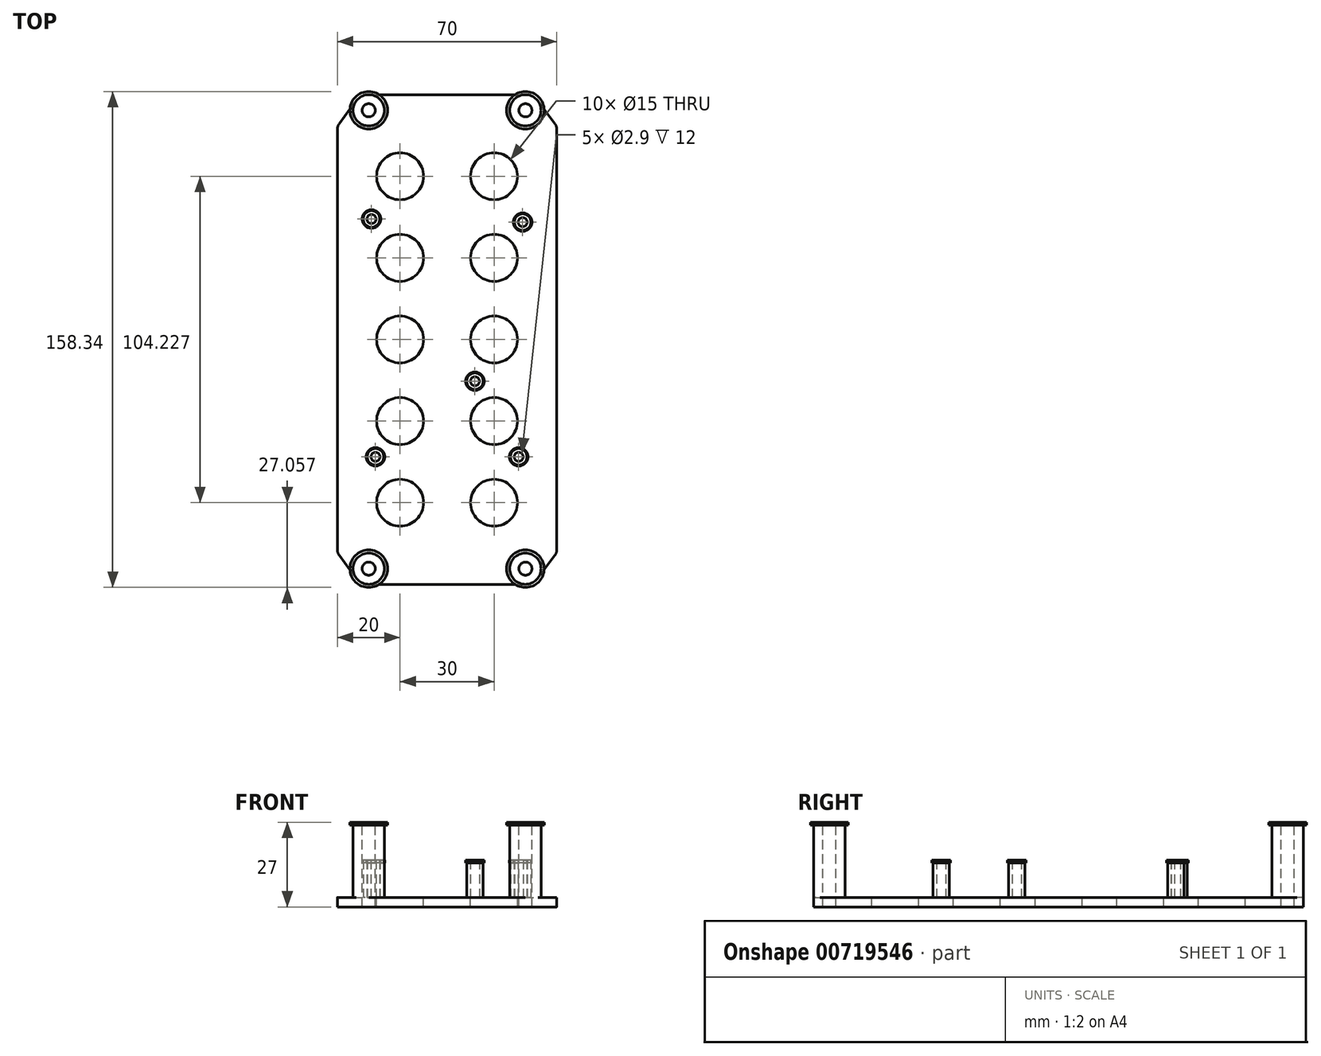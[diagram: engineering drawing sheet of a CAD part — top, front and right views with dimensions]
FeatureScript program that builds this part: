
annotation { "Feature Type Name" : "Feature", "Feature Type Description" : "" }
export const myFeature = defineFeature(function(context is Context, id is Id, definition is map)
    precondition{}
    {
        {
            var Q0;
            Q0=qCreatedBy(makeId("Top.planeOp"),FACE);
            var sketch = newSketch(context, id + "F0", { "sketchPlane" : qUnion([Q0])});
            skLineSegment(sketch, "E0.bottom", {"start": v(0, 0) * mm, "end": v(70, 0) * mm});
            skLineSegment(sketch, "E0.top", {"start": v(0, 136.34) * mm, "end": v(70, 136.34) * mm});
            skLineSegment(sketch, "E0.left", {"start": v(0, 0) * mm, "end": v(0, 136.34) * mm});
            skLineSegment(sketch, "E0.right", {"start": v(70, 0) * mm, "end": v(70, 136.34) * mm});
            skPoint(sketch, "E1", {"position": v(10.87, 106.64) * mm});
            skPoint(sketch, "E2", {"position": v(59.13, 105.64) * mm});
            skPoint(sketch, "E3", {"position": v(43.9, 54.84) * mm});
            skPoint(sketch, "E4", {"position": v(57.86, 30.71) * mm});
            skPoint(sketch, "E5", {"position": v(12.14, 30.71) * mm});
            skCircle(sketch, "E6", {"center": v(10.87, 106.64) * mm, "radius": 2.65 * mm});
            skCircle(sketch, "E7", {"center": v(59.13, 105.64) * mm, "radius": 2.65 * mm});
            skCircle(sketch, "E8", {"center": v(43.9, 54.84) * mm, "radius": 2.65 * mm});
            skCircle(sketch, "E9", {"center": v(12.14, 30.71) * mm, "radius": 2.65 * mm});
            skCircle(sketch, "E10", {"center": v(57.86, 30.71) * mm, "radius": 2.65 * mm});
            skCircle(sketch, "E11", {"center": v(10.87, 106.64) * mm, "radius": 1.45 * mm});
            skCircle(sketch, "E12", {"center": v(59.13, 105.64) * mm, "radius": 1.45 * mm});
            skCircle(sketch, "E13", {"center": v(43.9, 54.84) * mm, "radius": 1.45 * mm});
            skCircle(sketch, "E14", {"center": v(57.86, 30.71) * mm, "radius": 1.45 * mm});
            skCircle(sketch, "E15", {"center": v(12.14, 30.71) * mm, "radius": 1.45 * mm});
            skLineSegment(sketch, "E16.bottom", {"start": v(10.87, 106.64) * mm, "end": v(0, 106.64) * mm});
            skLineSegment(sketch, "E16.top", {"start": v(10.87, 106.64) * mm, "end": v(0, 106.64) * mm});
            skLineSegment(sketch, "E16.left", {"start": v(10.87, 106.64) * mm, "end": v(10.87, 106.64) * mm});
            skLineSegment(sketch, "E16.right", {"start": v(0, 106.64) * mm, "end": v(0, 106.64) * mm});
            skLineSegment(sketch, "E17", {"start": v(59.13, 105.64) * mm, "end": v(70, 105.64) * mm});
            skLineSegment(sketch, "E18", {"start": v(12.14, 30.71) * mm, "end": v(0, 30.71) * mm});
            skLineSegment(sketch, "E19", {"start": v(57.86, 30.71) * mm, "end": v(70, 30.71) * mm});
            skCircle(sketch, "E20", {"center": v(10, 141.34) * mm, "radius": 5 * mm});
            skCircle(sketch, "E21", {"center": v(60, 141.34) * mm, "radius": 5 * mm});
            skLineSegment(sketch, "E22", {"start": v(0, 136.34) * mm, "end": v(6, 144.34) * mm});
            skLineSegment(sketch, "E23", {"start": v(70, 136.34) * mm, "end": v(64, 144.34) * mm});
            skLineSegment(sketch, "E24", {"start": v(10, 146.34) * mm, "end": v(60, 146.34) * mm});
            skCircle(sketch, "E25", {"center": v(10, -5) * mm, "radius": 5 * mm});
            skCircle(sketch, "E26", {"center": v(60, -5) * mm, "radius": 5 * mm});
            skLineSegment(sketch, "E27", {"start": v(0, 0) * mm, "end": v(6, -8) * mm});
            skLineSegment(sketch, "E28", {"start": v(70, 0) * mm, "end": v(64, -8) * mm});
            skLineSegment(sketch, "E29", {"start": v(10, -10) * mm, "end": v(60, -10) * mm});
            skCircle(sketch, "E30", {"center": v(10, 141.34) * mm, "radius": 2.1 * mm});
            skCircle(sketch, "E31", {"center": v(60, 141.34) * mm, "radius": 2.1 * mm});
            skCircle(sketch, "E32", {"center": v(10, -5) * mm, "radius": 2.1 * mm});
            skCircle(sketch, "E33", {"center": v(60, -5) * mm, "radius": 2.1 * mm});
            skSolve(sketch);
        }
        {
            var Q0;
            Q0=makeQuery(id+"F0.imprint","IMPRINT",FACE,{"disambiguationData":[TD([[makeQuery(id+"F0.imprint","IMPRINT",EDGE,{"derivedFrom":sQuery(id+"F0.wireOp",EDGE,"5M5isl8t-deyZ-40FD-1slN-9rMmY2fGWf6l")}),-1.0]])]});
            var Q1;
            {var subQ1=sQuery(id+"F0.wireOp",EDGE,"E0.left");Q1=makeQuery(id+"F0.imprint","IMPRINT",FACE,{"disambiguationData":[TD([[makeQuery(id+"F0.imprint","IMPRINT",EDGE,{"derivedFrom":subQ1}),-1.0]])]});}
            var Q2;
            {var subQ0=sQuery(id+"F0.wireOp",EDGE,"ZGELtEtJ-xnq0-4358-XdRx-OSzrZUhgYs4m");Q2=makeQuery(id+"F0.imprint","IMPRINT",FACE,{"disambiguationData":[TD([[makeQuery(id+"F0.imprint","IMPRINT",EDGE,{"derivedFrom":subQ0}),-1.0]])]});}
            var Q3;
            {var subQ0=sQuery(id+"F0.wireOp",EDGE,"XsqxNTd2-7exo-Mk4u-Frq7-MKPhXaLccWfz");Q3=makeQuery(id+"F0.imprint","IMPRINT",FACE,{"disambiguationData":[TD([[makeQuery(id+"F0.imprint","IMPRINT",EDGE,{"derivedFrom":subQ0}),-1.0]])]});}
            var Q4;
            {var subQ0=sQuery(id+"F0.wireOp",EDGE,"Y27PalPK-6cuN-ouRf-MoMI-afCK04gGz7O5");Q4=makeQuery(id+"F0.imprint","IMPRINT",FACE,{"disambiguationData":[TD([[makeQuery(id+"F0.imprint","IMPRINT",EDGE,{"derivedFrom":subQ0}),1.0]])]});}
            var Q5;
            Q5=makeQuery(id+"F0.imprint","IMPRINT",FACE,{"disambiguationData":[TD([[makeQuery(id+"F0.imprint","IMPRINT",EDGE,{"derivedFrom":sQuery(id+"F0.wireOp",EDGE,"YguYaOqL-j1yr-7eBz-XWkk-AffqH1J2VJiA")}),-1.0]])]});
            var Q6;
            {var subQ0=sQuery(id+"F0.wireOp",EDGE,"ZxH4SoS6-8SnG-QbFF-Vepe-AWZUzMMQzlqZ");Q6=makeQuery(id+"F0.imprint","IMPRINT",FACE,{"disambiguationData":[TD([[makeQuery(id+"F0.imprint","IMPRINT",EDGE,{"derivedFrom":subQ0}),-1.0]])]});}
            var Q7;
            Q7=makeQuery(id+"F0.imprint","IMPRINT",FACE,{"disambiguationData":[TD([[makeQuery(id+"F0.imprint","IMPRINT",EDGE,{"derivedFrom":sQuery(id+"F0.wireOp",EDGE,"E9")}),1.0]])]});
            var Q8;
            Q8=makeQuery(id+"F0.imprint","IMPRINT",FACE,{"disambiguationData":[TD([[makeQuery(id+"F0.imprint","IMPRINT",EDGE,{"derivedFrom":sQuery(id+"F0.wireOp",EDGE,"E7")}),1.0]])]});
            var Q9;
            Q9=makeQuery(id+"F0.imprint","IMPRINT",FACE,{"disambiguationData":[TD([[makeQuery(id+"F0.imprint","IMPRINT",EDGE,{"derivedFrom":sQuery(id+"F0.wireOp",EDGE,"E8")}),1.0]])]});
            var Q10;
            Q10=makeQuery(id+"F0.imprint","IMPRINT",FACE,{"disambiguationData":[TD([[makeQuery(id+"F0.imprint","IMPRINT",EDGE,{"derivedFrom":sQuery(id+"F0.wireOp",EDGE,"E10")}),1.0]])]});
            var Q11;
            Q11=makeQuery(id+"F0.imprint","IMPRINT",FACE,{"disambiguationData":[TD([[makeQuery(id+"F0.imprint","IMPRINT",EDGE,{"derivedFrom":sQuery(id+"F0.wireOp",EDGE,"E6")}),1.0]])]});
            var Q12;
            Q12=makeQuery(id+"F0.imprint","IMPRINT",FACE,{"disambiguationData":[TD([[makeQuery(id+"F0.imprint","IMPRINT",EDGE,{"derivedFrom":sQuery(id+"F0.wireOp",EDGE,"E11")}),1.0]])]});
            var Q13;
            Q13=makeQuery(id+"F0.imprint","IMPRINT",FACE,{"disambiguationData":[TD([[makeQuery(id+"F0.imprint","IMPRINT",EDGE,{"derivedFrom":sQuery(id+"F0.wireOp",EDGE,"E15")}),1.0]])]});
            var Q14;
            Q14=makeQuery(id+"F0.imprint","IMPRINT",FACE,{"disambiguationData":[TD([[makeQuery(id+"F0.imprint","IMPRINT",EDGE,{"derivedFrom":sQuery(id+"F0.wireOp",EDGE,"E12")}),1.0]])]});
            var Q15;
            Q15=makeQuery(id+"F0.imprint","IMPRINT",FACE,{"disambiguationData":[TD([[makeQuery(id+"F0.imprint","IMPRINT",EDGE,{"derivedFrom":sQuery(id+"F0.wireOp",EDGE,"E14")}),1.0]])]});
            var Q16;
            Q16=makeQuery(id+"F0.imprint","IMPRINT",FACE,{"disambiguationData":[TD([[makeQuery(id+"F0.imprint","IMPRINT",EDGE,{"derivedFrom":sQuery(id+"F0.wireOp",EDGE,"E13")}),1.0]])]});
            var Q17;
            {var subQ5=sQuery(id+"F0.wireOp",EDGE,"E24");Q17=makeQuery(id+"F0.imprint","IMPRINT",FACE,{"disambiguationData":[TD([[makeQuery(id+"F0.imprint","IMPRINT",EDGE,{"derivedFrom":subQ5}),-1.0]])]});}
            var Q18;
            {var subQ0=sQuery(id+"F0.wireOp",EDGE,"E22");Q18=makeQuery(id+"F0.imprint","IMPRINT",FACE,{"disambiguationData":[TD([[makeQuery(id+"F0.imprint","IMPRINT",EDGE,{"derivedFrom":subQ0}),-1.0]])]});}
            var Q19;
            {var subQ0=sQuery(id+"F0.wireOp",EDGE,"E20");var subQ1=makeQuery(id+"F0.imprint","INTERSECT",VERTEX,{"derivedFrom":[subQ0,sQuery(id+"F0.wireOp",EDGE,"E22")]});Q19=makeQuery(id+"F0.imprint","IMPRINT",FACE,{"disambiguationData":[TD([[makeQuery(id+"F0.imprint","IMPRINT",EDGE,{"disambiguationData":[TD([[subQ1,1.0]])],"derivedFrom":subQ0}),1.0]])]});}
            var Q20;
            {var subQ0=sQuery(id+"F0.wireOp",EDGE,"E21");var subQ1=makeQuery(id+"F0.imprint","INTERSECT",VERTEX,{"derivedFrom":[subQ0,sQuery(id+"F0.wireOp",EDGE,"E23")]});Q20=makeQuery(id+"F0.imprint","IMPRINT",FACE,{"disambiguationData":[TD([[makeQuery(id+"F0.imprint","IMPRINT",EDGE,{"disambiguationData":[TD([[subQ1,-1.0]])],"derivedFrom":subQ0}),1.0]])]});}
            var Q21;
            {var subQ0=sQuery(id+"F0.wireOp",EDGE,"E23");Q21=makeQuery(id+"F0.imprint","IMPRINT",FACE,{"disambiguationData":[TD([[makeQuery(id+"F0.imprint","IMPRINT",EDGE,{"derivedFrom":subQ0}),1.0]])]});}
            var Q22;
            {var subQ0=sQuery(id+"F0.wireOp",EDGE,"E28");Q22=makeQuery(id+"F0.imprint","IMPRINT",FACE,{"disambiguationData":[TD([[makeQuery(id+"F0.imprint","IMPRINT",EDGE,{"derivedFrom":subQ0}),-1.0]])]});}
            var Q23;
            {var subQ0=sQuery(id+"F0.wireOp",EDGE,"E26");var subQ1=makeQuery(id+"F0.imprint","INTERSECT",VERTEX,{"derivedFrom":[subQ0,sQuery(id+"F0.wireOp",EDGE,"E29")]});Q23=makeQuery(id+"F0.imprint","IMPRINT",FACE,{"disambiguationData":[TD([[makeQuery(id+"F0.imprint","IMPRINT",EDGE,{"disambiguationData":[TD([[subQ1,1.0]])],"derivedFrom":subQ0}),1.0]])]});}
            var Q24;
            {var subQ5=sQuery(id+"F0.wireOp",EDGE,"E29");Q24=makeQuery(id+"F0.imprint","IMPRINT",FACE,{"disambiguationData":[TD([[makeQuery(id+"F0.imprint","IMPRINT",EDGE,{"derivedFrom":subQ5}),1.0]])]});}
            var Q25;
            {var subQ0=sQuery(id+"F0.wireOp",EDGE,"E25");var subQ1=makeQuery(id+"F0.imprint","INTERSECT",VERTEX,{"derivedFrom":[subQ0,sQuery(id+"F0.wireOp",EDGE,"E27")]});Q25=makeQuery(id+"F0.imprint","IMPRINT",FACE,{"disambiguationData":[TD([[makeQuery(id+"F0.imprint","IMPRINT",EDGE,{"disambiguationData":[TD([[subQ1,1.0]])],"derivedFrom":subQ0}),1.0]])]});}
            var Q26;
            {var subQ0=sQuery(id+"F0.wireOp",EDGE,"E27");Q26=makeQuery(id+"F0.imprint","IMPRINT",FACE,{"disambiguationData":[TD([[makeQuery(id+"F0.imprint","IMPRINT",EDGE,{"derivedFrom":subQ0}),1.0]])]});}
            extrude(context, id + "F1", {"entities" : qUnion([Q0, Q1, Q2, Q3, Q4, Q5, Q6, Q7, Q8, Q9, Q10, Q11, Q12, Q13, Q14, Q15, Q16, Q17, Q18, Q19, Q20, Q21, Q22, Q23, Q24, Q25, Q26]), "oppositeDirection" : true, "depth" : 3 * mm, "offsetDistance" : 25 * mm});
        }
        {
            var Q0;
            Q0=makeQuery(id+"F0.imprint","IMPRINT",FACE,{"disambiguationData":[TD([[makeQuery(id+"F0.imprint","IMPRINT",EDGE,{"derivedFrom":sQuery(id+"F0.wireOp",EDGE,"E9")}),1.0]])]});
            var Q1;
            Q1=makeQuery(id+"F0.imprint","IMPRINT",FACE,{"disambiguationData":[TD([[makeQuery(id+"F0.imprint","IMPRINT",EDGE,{"derivedFrom":sQuery(id+"F0.wireOp",EDGE,"E8")}),1.0]])]});
            var Q2;
            Q2=makeQuery(id+"F0.imprint","IMPRINT",FACE,{"disambiguationData":[TD([[makeQuery(id+"F0.imprint","IMPRINT",EDGE,{"derivedFrom":sQuery(id+"F0.wireOp",EDGE,"E10")}),1.0]])]});
            var Q3;
            Q3=makeQuery(id+"F0.imprint","IMPRINT",FACE,{"disambiguationData":[TD([[makeQuery(id+"F0.imprint","IMPRINT",EDGE,{"derivedFrom":sQuery(id+"F0.wireOp",EDGE,"E6")}),1.0]])]});
            var Q4;
            Q4=makeQuery(id+"F0.imprint","IMPRINT",FACE,{"disambiguationData":[TD([[makeQuery(id+"F0.imprint","IMPRINT",EDGE,{"derivedFrom":sQuery(id+"F0.wireOp",EDGE,"E7")}),1.0]])]});
            extrude(context, id + "F2", {"entities" : qUnion([Q0, Q1, Q2, Q3, Q4]), "operationType" : NewBodyOperationType.ADD, "depth" : 12 * mm, "offsetDistance" : 25 * mm});
        }
        {
            var Q0;
            Q0=makeQuery(id+"F0.imprint","IMPRINT",FACE,{"disambiguationData":[TD([[makeQuery(id+"F0.imprint","IMPRINT",EDGE,{"derivedFrom":sQuery(id+"F0.wireOp",EDGE,"E30")}),-1.0]])]});
            var Q1;
            Q1=makeQuery(id+"F0.imprint","IMPRINT",FACE,{"disambiguationData":[TD([[makeQuery(id+"F0.imprint","IMPRINT",EDGE,{"derivedFrom":sQuery(id+"F0.wireOp",EDGE,"E31")}),-1.0]])]});
            var Q2;
            Q2=makeQuery(id+"F0.imprint","IMPRINT",FACE,{"disambiguationData":[TD([[makeQuery(id+"F0.imprint","IMPRINT",EDGE,{"derivedFrom":sQuery(id+"F0.wireOp",EDGE,"E32")}),-1.0]])]});
            var Q3;
            Q3=makeQuery(id+"F0.imprint","IMPRINT",FACE,{"disambiguationData":[TD([[makeQuery(id+"F0.imprint","IMPRINT",EDGE,{"derivedFrom":sQuery(id+"F0.wireOp",EDGE,"E33")}),-1.0]])]});
            extrude(context, id + "F3", {"entities" : qUnion([Q0, Q1, Q2, Q3]), "operationType" : NewBodyOperationType.ADD, "depth" : 24 * mm, "offsetDistance" : 25 * mm});
        }
        {
            var Q0;
            Q0=qCreatedBy(makeId("Top.planeOp"),FACE);
            var sketch = newSketch(context, id + "F4", { "sketchPlane" : qUnion([Q0])});
            skLineSegment(sketch, "E34.0", {"start": v(0, 136.34) * mm, "end": v(70, 136.34) * mm});
            skLineSegment(sketch, "E35.0", {"start": v(0, 0) * mm, "end": v(0, 136.34) * mm});
            skLineSegment(sketch, "E36.0", {"start": v(70, 0) * mm, "end": v(70, 136.34) * mm});
            skPoint(sketch, "E37", {"position": v(20, 120.28) * mm});
            skPoint(sketch, "E38", {"position": v(50, 120.28) * mm});
            skPoint(sketch, "E39", {"position": v(50, 68.17) * mm});
            skPoint(sketch, "E40", {"position": v(50, 42.11) * mm});
            skPoint(sketch, "E41", {"position": v(20, 68.17) * mm});
            skPoint(sketch, "E42", {"position": v(20, 42.11) * mm});
            skPoint(sketch, "E43", {"position": v(20, 16.06) * mm});
            skPoint(sketch, "E44", {"position": v(50, 16.06) * mm});
            skLineSegment(sketch, "E45", {"start": v(20, 68.17) * mm, "end": v(20, 42.11) * mm});
            skLineSegment(sketch, "E46", {"start": v(20, 42.11) * mm, "end": v(20, 16.06) * mm});
            skLineSegment(sketch, "E47", {"start": v(50, 16.06) * mm, "end": v(50, 42.11) * mm});
            skLineSegment(sketch, "E48", {"start": v(50, 68.17) * mm, "end": v(50, 42.11) * mm});
            skPoint(sketch, "E49", {"position": v(20, 94.23) * mm});
            skPoint(sketch, "E50", {"position": v(50, 94.23) * mm});
            skLineSegment(sketch, "E51", {"start": v(50, 120.28) * mm, "end": v(50, 94.23) * mm});
            skLineSegment(sketch, "E52", {"start": v(50, 68.17) * mm, "end": v(50, 94.23) * mm});
            skLineSegment(sketch, "E53", {"start": v(20, 94.23) * mm, "end": v(20, 68.17) * mm});
            skLineSegment(sketch, "E54", {"start": v(20, 94.23) * mm, "end": v(20, 120.28) * mm});
            skCircle(sketch, "E55", {"center": v(20, 120.28) * mm, "radius": 7.5 * mm});
            skCircle(sketch, "E56", {"center": v(50, 120.28) * mm, "radius": 7.5 * mm});
            skCircle(sketch, "E57", {"center": v(50, 94.23) * mm, "radius": 7.5 * mm});
            skCircle(sketch, "E58", {"center": v(20, 94.23) * mm, "radius": 7.5 * mm});
            skCircle(sketch, "E59", {"center": v(20, 68.17) * mm, "radius": 7.5 * mm});
            skCircle(sketch, "E60", {"center": v(50, 68.17) * mm, "radius": 7.5 * mm});
            skCircle(sketch, "E61", {"center": v(20, 42.11) * mm, "radius": 7.5 * mm});
            skCircle(sketch, "E62", {"center": v(50, 42.11) * mm, "radius": 7.5 * mm});
            skCircle(sketch, "E63", {"center": v(20, 16.06) * mm, "radius": 7.5 * mm});
            skCircle(sketch, "E64", {"center": v(50, 16.06) * mm, "radius": 7.5 * mm});
            skLineSegment(sketch, "E65", {"start": v(50, 120.28) * mm, "end": v(50, 146.34) * mm});
            skLineSegment(sketch, "E66", {"start": v(20, 120.28) * mm, "end": v(20, 146.34) * mm});
            skLineSegment(sketch, "E67", {"start": v(50, 16.06) * mm, "end": v(50, -10) * mm});
            skLineSegment(sketch, "E68", {"start": v(20, 16.06) * mm, "end": v(20, -10) * mm});
            skLineSegment(sketch, "E69", {"start": v(0, 0) * mm, "end": v(20, 0) * mm});
            skLineSegment(sketch, "E70", {"start": v(70, 0) * mm, "end": v(50, 0) * mm});
            skLineSegment(sketch, "E71.0", {"start": v(10, 146.34) * mm, "end": v(60, 146.34) * mm});
            skLineSegment(sketch, "E71.1", {"start": v(10, -10) * mm, "end": v(60, -10) * mm});
            skSolve(sketch);
        }
        {
            var Q0;
            {var subQ0=sQuery(id+"F4.wireOp",EDGE,"E65");var subQ1=sQuery(id+"F4.wireOp",EDGE,"E51");var subQ2=makeQuery(id+"F4.imprint","INTERSECT",VERTEX,{"derivedFrom":[subQ1,subQ0]});Q0=makeQuery(id+"F4.imprint","IMPRINT",FACE,{"disambiguationData":[TD([[makeQuery(id+"F4.imprint","IMPRINT",EDGE,{"disambiguationData":[TD([[subQ2,-1.0]])],"derivedFrom":subQ1}),-1.0]])]});}
            var Q1;
            {var subQ0=sQuery(id+"F4.wireOp",EDGE,"E65");var subQ1=sQuery(id+"F4.wireOp",EDGE,"E51");var subQ2=makeQuery(id+"F4.imprint","INTERSECT",VERTEX,{"derivedFrom":[subQ1,subQ0]});Q1=makeQuery(id+"F4.imprint","IMPRINT",FACE,{"disambiguationData":[TD([[makeQuery(id+"F4.imprint","IMPRINT",EDGE,{"disambiguationData":[TD([[subQ2,-1.0]])],"derivedFrom":subQ1}),1.0]])]});}
            var Q2;
            {var subQ0=sQuery(id+"F4.wireOp",EDGE,"E66");var subQ1=sQuery(id+"F4.wireOp",EDGE,"E54");var subQ2=makeQuery(id+"F4.imprint","INTERSECT",VERTEX,{"derivedFrom":[subQ1,subQ0]});Q2=makeQuery(id+"F4.imprint","IMPRINT",FACE,{"disambiguationData":[TD([[makeQuery(id+"F4.imprint","IMPRINT",EDGE,{"disambiguationData":[TD([[subQ2,1.0]])],"derivedFrom":subQ1}),-1.0]])]});}
            var Q3;
            {var subQ0=sQuery(id+"F4.wireOp",EDGE,"E66");var subQ1=sQuery(id+"F4.wireOp",EDGE,"E54");var subQ2=makeQuery(id+"F4.imprint","INTERSECT",VERTEX,{"derivedFrom":[subQ1,subQ0]});Q3=makeQuery(id+"F4.imprint","IMPRINT",FACE,{"disambiguationData":[TD([[makeQuery(id+"F4.imprint","IMPRINT",EDGE,{"disambiguationData":[TD([[subQ2,1.0]])],"derivedFrom":subQ1}),1.0]])]});}
            var Q4;
            {var subQ0=sQuery(id+"F4.wireOp",EDGE,"E54");var subQ1=sQuery(id+"F4.wireOp",EDGE,"E53");var subQ2=makeQuery(id+"F4.imprint","INTERSECT",VERTEX,{"derivedFrom":[subQ1,subQ0]});Q4=makeQuery(id+"F4.imprint","IMPRINT",FACE,{"disambiguationData":[TD([[makeQuery(id+"F4.imprint","IMPRINT",EDGE,{"disambiguationData":[TD([[subQ2,-1.0]])],"derivedFrom":subQ1}),-1.0]])]});}
            var Q5;
            {var subQ0=sQuery(id+"F4.wireOp",EDGE,"E54");var subQ1=sQuery(id+"F4.wireOp",EDGE,"E53");var subQ2=makeQuery(id+"F4.imprint","INTERSECT",VERTEX,{"derivedFrom":[subQ1,subQ0]});Q5=makeQuery(id+"F4.imprint","IMPRINT",FACE,{"disambiguationData":[TD([[makeQuery(id+"F4.imprint","IMPRINT",EDGE,{"disambiguationData":[TD([[subQ2,-1.0]])],"derivedFrom":subQ1}),1.0]])]});}
            var Q6;
            {var subQ0=sQuery(id+"F4.wireOp",EDGE,"E52");var subQ1=sQuery(id+"F4.wireOp",EDGE,"E51");var subQ2=makeQuery(id+"F4.imprint","INTERSECT",VERTEX,{"derivedFrom":[subQ1,subQ0]});Q6=makeQuery(id+"F4.imprint","IMPRINT",FACE,{"disambiguationData":[TD([[makeQuery(id+"F4.imprint","IMPRINT",EDGE,{"disambiguationData":[TD([[subQ2,1.0]])],"derivedFrom":subQ1}),-1.0]])]});}
            var Q7;
            {var subQ0=sQuery(id+"F4.wireOp",EDGE,"E52");var subQ1=sQuery(id+"F4.wireOp",EDGE,"E51");var subQ2=makeQuery(id+"F4.imprint","INTERSECT",VERTEX,{"derivedFrom":[subQ1,subQ0]});Q7=makeQuery(id+"F4.imprint","IMPRINT",FACE,{"disambiguationData":[TD([[makeQuery(id+"F4.imprint","IMPRINT",EDGE,{"disambiguationData":[TD([[subQ2,1.0]])],"derivedFrom":subQ1}),1.0]])]});}
            var Q8;
            {var subQ0=sQuery(id+"F4.wireOp",EDGE,"E52");var subQ1=sQuery(id+"F4.wireOp",EDGE,"E48");var subQ2=makeQuery(id+"F4.imprint","INTERSECT",VERTEX,{"derivedFrom":[subQ1,subQ0]});Q8=makeQuery(id+"F4.imprint","IMPRINT",FACE,{"disambiguationData":[TD([[makeQuery(id+"F4.imprint","IMPRINT",EDGE,{"disambiguationData":[TD([[subQ2,-1.0]])],"derivedFrom":subQ1}),-1.0]])]});}
            var Q9;
            {var subQ0=sQuery(id+"F4.wireOp",EDGE,"E52");var subQ1=sQuery(id+"F4.wireOp",EDGE,"E48");var subQ2=makeQuery(id+"F4.imprint","INTERSECT",VERTEX,{"derivedFrom":[subQ1,subQ0]});Q9=makeQuery(id+"F4.imprint","IMPRINT",FACE,{"disambiguationData":[TD([[makeQuery(id+"F4.imprint","IMPRINT",EDGE,{"disambiguationData":[TD([[subQ2,-1.0]])],"derivedFrom":subQ1}),1.0]])]});}
            var Q10;
            {var subQ0=sQuery(id+"F4.wireOp",EDGE,"E53");var subQ1=sQuery(id+"F4.wireOp",EDGE,"E45");var subQ2=makeQuery(id+"F4.imprint","INTERSECT",VERTEX,{"derivedFrom":[subQ1,subQ0]});Q10=makeQuery(id+"F4.imprint","IMPRINT",FACE,{"disambiguationData":[TD([[makeQuery(id+"F4.imprint","IMPRINT",EDGE,{"disambiguationData":[TD([[subQ2,-1.0]])],"derivedFrom":subQ1}),1.0]])]});}
            var Q11;
            {var subQ0=sQuery(id+"F4.wireOp",EDGE,"E53");var subQ1=sQuery(id+"F4.wireOp",EDGE,"E45");var subQ2=makeQuery(id+"F4.imprint","INTERSECT",VERTEX,{"derivedFrom":[subQ1,subQ0]});Q11=makeQuery(id+"F4.imprint","IMPRINT",FACE,{"disambiguationData":[TD([[makeQuery(id+"F4.imprint","IMPRINT",EDGE,{"disambiguationData":[TD([[subQ2,-1.0]])],"derivedFrom":subQ1}),-1.0]])]});}
            var Q12;
            {var subQ0=sQuery(id+"F4.wireOp",EDGE,"E46");var subQ1=sQuery(id+"F4.wireOp",EDGE,"E45");var subQ2=makeQuery(id+"F4.imprint","INTERSECT",VERTEX,{"derivedFrom":[subQ1,subQ0]});Q12=makeQuery(id+"F4.imprint","IMPRINT",FACE,{"disambiguationData":[TD([[makeQuery(id+"F4.imprint","IMPRINT",EDGE,{"disambiguationData":[TD([[subQ2,1.0]])],"derivedFrom":subQ1}),-1.0]])]});}
            var Q13;
            {var subQ0=sQuery(id+"F4.wireOp",EDGE,"E46");var subQ1=sQuery(id+"F4.wireOp",EDGE,"E45");var subQ2=makeQuery(id+"F4.imprint","INTERSECT",VERTEX,{"derivedFrom":[subQ1,subQ0]});Q13=makeQuery(id+"F4.imprint","IMPRINT",FACE,{"disambiguationData":[TD([[makeQuery(id+"F4.imprint","IMPRINT",EDGE,{"disambiguationData":[TD([[subQ2,1.0]])],"derivedFrom":subQ1}),1.0]])]});}
            var Q14;
            {var subQ0=sQuery(id+"F4.wireOp",EDGE,"E48");var subQ1=sQuery(id+"F4.wireOp",EDGE,"E47");var subQ2=makeQuery(id+"F4.imprint","INTERSECT",VERTEX,{"derivedFrom":[subQ1,subQ0]});Q14=makeQuery(id+"F4.imprint","IMPRINT",FACE,{"disambiguationData":[TD([[makeQuery(id+"F4.imprint","IMPRINT",EDGE,{"disambiguationData":[TD([[subQ2,1.0]])],"derivedFrom":subQ1}),1.0]])]});}
            var Q15;
            {var subQ0=sQuery(id+"F4.wireOp",EDGE,"E48");var subQ1=sQuery(id+"F4.wireOp",EDGE,"E47");var subQ2=makeQuery(id+"F4.imprint","INTERSECT",VERTEX,{"derivedFrom":[subQ1,subQ0]});Q15=makeQuery(id+"F4.imprint","IMPRINT",FACE,{"disambiguationData":[TD([[makeQuery(id+"F4.imprint","IMPRINT",EDGE,{"disambiguationData":[TD([[subQ2,1.0]])],"derivedFrom":subQ1}),-1.0]])]});}
            var Q16;
            {var subQ0=sQuery(id+"F4.wireOp",EDGE,"E67");var subQ1=sQuery(id+"F4.wireOp",EDGE,"E47");var subQ2=makeQuery(id+"F4.imprint","INTERSECT",VERTEX,{"derivedFrom":[subQ1,subQ0]});Q16=makeQuery(id+"F4.imprint","IMPRINT",FACE,{"disambiguationData":[TD([[makeQuery(id+"F4.imprint","IMPRINT",EDGE,{"disambiguationData":[TD([[subQ2,-1.0]])],"derivedFrom":subQ1}),-1.0]])]});}
            var Q17;
            {var subQ0=sQuery(id+"F4.wireOp",EDGE,"E67");var subQ1=sQuery(id+"F4.wireOp",EDGE,"E47");var subQ2=makeQuery(id+"F4.imprint","INTERSECT",VERTEX,{"derivedFrom":[subQ1,subQ0]});Q17=makeQuery(id+"F4.imprint","IMPRINT",FACE,{"disambiguationData":[TD([[makeQuery(id+"F4.imprint","IMPRINT",EDGE,{"disambiguationData":[TD([[subQ2,-1.0]])],"derivedFrom":subQ1}),1.0]])]});}
            var Q18;
            {var subQ0=sQuery(id+"F4.wireOp",EDGE,"E68");var subQ1=sQuery(id+"F4.wireOp",EDGE,"E46");var subQ2=makeQuery(id+"F4.imprint","INTERSECT",VERTEX,{"derivedFrom":[subQ1,subQ0]});Q18=makeQuery(id+"F4.imprint","IMPRINT",FACE,{"disambiguationData":[TD([[makeQuery(id+"F4.imprint","IMPRINT",EDGE,{"disambiguationData":[TD([[subQ2,1.0]])],"derivedFrom":subQ1}),1.0]])]});}
            var Q19;
            {var subQ0=sQuery(id+"F4.wireOp",EDGE,"E68");var subQ1=sQuery(id+"F4.wireOp",EDGE,"E46");var subQ2=makeQuery(id+"F4.imprint","INTERSECT",VERTEX,{"derivedFrom":[subQ1,subQ0]});Q19=makeQuery(id+"F4.imprint","IMPRINT",FACE,{"disambiguationData":[TD([[makeQuery(id+"F4.imprint","IMPRINT",EDGE,{"disambiguationData":[TD([[subQ2,1.0]])],"derivedFrom":subQ1}),-1.0]])]});}
            var Q20;
            Q20=sQuery(id+"F4.wireOp",EDGE,"E55");
            var Q21;
            Q21=sQuery(id+"F4.wireOp",EDGE,"E56");
            var Q22;
            Q22=sQuery(id+"F4.wireOp",EDGE,"E57");
            var Q23;
            Q23=sQuery(id+"F4.wireOp",EDGE,"E58");
            var Q24;
            Q24=sQuery(id+"F4.wireOp",EDGE,"E60");
            var Q25;
            Q25=sQuery(id+"F4.wireOp",EDGE,"E59");
            var Q26;
            Q26=sQuery(id+"F4.wireOp",EDGE,"E61");
            var Q27;
            Q27=sQuery(id+"F4.wireOp",EDGE,"E62");
            var Q28;
            Q28=sQuery(id+"F4.wireOp",EDGE,"E63");
            var Q29;
            Q29=sQuery(id+"F4.wireOp",EDGE,"E64");
            extrude(context, id + "F5", {"entities" : qUnion([Q0, Q1, Q2, Q3, Q4, Q5, Q6, Q7, Q8, Q9, Q10, Q11, Q12, Q13, Q14, Q15, Q16, Q17, Q18, Q19]), "operationType" : NewBodyOperationType.REMOVE, "surfaceEntities" : qUnion([Q20, Q21, Q22, Q23, Q24, Q25, Q26, Q27, Q28, Q29]), "endBound" : BoundingType.THROUGH_ALL, "oppositeDirection" : true, "depth" : 25 * mm, "offsetDistance" : 25 * mm});
        }
        {
            var Q0;
            Q0=qCreatedBy(makeId("Top.planeOp"),FACE);
            var sketch = newSketch(context, id + "F6", { "sketchPlane" : qUnion([Q0])});
            skPoint(sketch, "E72.0", {"position": v(35, 146.34) * mm});
            skPoint(sketch, "E73.0", {"position": v(35, -10) * mm});
            skPoint(sketch, "E74.0", {"position": v(0, 68.17) * mm});
            skCircle(sketch, "E75.0", {"center": v(10, 141.34) * mm, "radius": 5 * mm});
            skCircle(sketch, "E76.0", {"center": v(60, 141.34) * mm, "radius": 5 * mm});
            skCircle(sketch, "E77.0", {"center": v(10, -5) * mm, "radius": 5 * mm});
            skCircle(sketch, "E78.0", {"center": v(60, -5) * mm, "radius": 5 * mm});
            skLineSegment(sketch, "E79", {"start": v(14.36, -2.56) * mm, "end": v(35, 9) * mm});
            skLineSegment(sketch, "E80", {"start": v(55.64, -2.56) * mm, "end": v(35, 9) * mm});
            skLineSegment(sketch, "E81", {"start": v(55.64, 138.9) * mm, "end": v(35, 127.34) * mm});
            skLineSegment(sketch, "E82", {"start": v(35, 127.34) * mm, "end": v(14.36, 138.9) * mm});
            skLineSegment(sketch, "E83", {"start": v(35, 146.34) * mm, "end": v(35, 127.34) * mm});
            skLineSegment(sketch, "E84", {"start": v(35, 127.34) * mm, "end": v(35, 9) * mm});
            skLineSegment(sketch, "E85", {"start": v(35, 9) * mm, "end": v(35, -10) * mm});
            skLineSegment(sketch, "E86", {"start": v(35, 127.34) * mm, "end": v(34.51, 126.47) * mm});
            skLineSegment(sketch, "E87", {"start": v(34.51, 126.47) * mm, "end": v(13.79, 138.07) * mm});
            skLineSegment(sketch, "E88", {"start": v(35, 127.34) * mm, "end": v(35.49, 128.21) * mm});
            skLineSegment(sketch, "E89", {"start": v(35.49, 128.21) * mm, "end": v(14.76, 139.82) * mm});
            skLineSegment(sketch, "E90", {"start": v(35, 127.34) * mm, "end": v(35.49, 126.47) * mm});
            skLineSegment(sketch, "E91", {"start": v(35.49, 126.47) * mm, "end": v(56.21, 138.07) * mm});
            skLineSegment(sketch, "E92", {"start": v(35, 127.34) * mm, "end": v(34.51, 128.21) * mm});
            skLineSegment(sketch, "E93", {"start": v(34.51, 128.21) * mm, "end": v(55.24, 139.82) * mm});
            skLineSegment(sketch, "E94", {"start": v(35, 9) * mm, "end": v(34.51, 9.87) * mm});
            skLineSegment(sketch, "E95", {"start": v(34.51, 9.87) * mm, "end": v(13.79, -1.73) * mm});
            skLineSegment(sketch, "E96", {"start": v(35, 9) * mm, "end": v(35.49, 8.13) * mm});
            skLineSegment(sketch, "E97", {"start": v(35.49, 8.13) * mm, "end": v(14.76, -3.48) * mm});
            skLineSegment(sketch, "E98", {"start": v(35, 9) * mm, "end": v(35.49, 9.87) * mm});
            skLineSegment(sketch, "E99", {"start": v(35.49, 9.87) * mm, "end": v(56.21, -1.73) * mm});
            skLineSegment(sketch, "E100", {"start": v(35, 9) * mm, "end": v(34.51, 8.13) * mm});
            skLineSegment(sketch, "E101", {"start": v(34.51, 8.13) * mm, "end": v(55.24, -3.48) * mm});
            skLineSegment(sketch, "E102", {"start": v(35, 127.34) * mm, "end": v(34, 127.34) * mm});
            skLineSegment(sketch, "E103", {"start": v(34, 127.34) * mm, "end": v(34, 9) * mm});
            skLineSegment(sketch, "E104", {"start": v(34, 9) * mm, "end": v(35, 9) * mm});
            skLineSegment(sketch, "E105", {"start": v(35, 9) * mm, "end": v(36, 9) * mm});
            skLineSegment(sketch, "E106", {"start": v(36, 9) * mm, "end": v(36, 127.34) * mm});
            skLineSegment(sketch, "E107", {"start": v(36, 127.34) * mm, "end": v(35, 127.34) * mm});
            skSolve(sketch);
        }
        {
            var Q0;
            Q0=makeQuery(id+"F2.opExtrude","CAP_FACE",FACE,{"disambiguationData":[OSD([sQuery(id+"F0.wireOp",EDGE,"E6"),sQuery(id+"F0.wireOp",EDGE,"E11")])],"isStart":false});
            var sketch = newSketch(context, id + "F7", { "sketchPlane" : qUnion([Q0])});
            skCircle(sketch, "E108.1.0", {"center": v(59.13, 105.64) * mm, "radius": 2.65 * mm});
            skCircle(sketch, "E108.2.0", {"center": v(43.9, 54.84) * mm, "radius": 2.65 * mm});
            skCircle(sketch, "E108.3.0", {"center": v(12.14, 30.71) * mm, "radius": 2.65 * mm});
            skCircle(sketch, "E108.4.0", {"center": v(57.86, 30.71) * mm, "radius": 2.65 * mm});
            skCircle(sketch, "E109", {"center": v(10.87, 106.64) * mm, "radius": 2.95 * mm});
            skCircle(sketch, "E110", {"center": v(59.13, 105.64) * mm, "radius": 2.95 * mm});
            skCircle(sketch, "E111", {"center": v(43.9, 54.84) * mm, "radius": 2.95 * mm});
            skCircle(sketch, "E112", {"center": v(12.14, 30.71) * mm, "radius": 2.95 * mm});
            skCircle(sketch, "E113", {"center": v(57.86, 30.71) * mm, "radius": 2.95 * mm});
            skSolve(sketch);
        }
        {
            var Q0;
            Q0=makeQuery(id+"F7.imprint","IMPRINT",FACE,{"disambiguationData":[TD([[makeQuery(id+"F7.imprint","IMPRINT",EDGE,{"derivedFrom":sQuery(id+"F7.wireOp",EDGE,"E108.1.0")}),-1.0]])]});
            var Q1;
            Q1=makeQuery(id+"F7.imprint","IMPRINT",FACE,{"disambiguationData":[TD([[makeQuery(id+"F7.imprint","IMPRINT",EDGE,{"derivedFrom":sQuery(id+"F7.wireOp",EDGE,"E109")}),1.0]])]});
            var Q2;
            Q2=makeQuery(id+"F7.imprint","IMPRINT",FACE,{"disambiguationData":[TD([[makeQuery(id+"F7.imprint","IMPRINT",EDGE,{"derivedFrom":sQuery(id+"F7.wireOp",EDGE,"E108.2.0")}),-1.0]])]});
            var Q3;
            Q3=makeQuery(id+"F7.imprint","IMPRINT",FACE,{"disambiguationData":[TD([[makeQuery(id+"F7.imprint","IMPRINT",EDGE,{"derivedFrom":sQuery(id+"F7.wireOp",EDGE,"E108.3.0")}),-1.0]])]});
            var Q4;
            Q4=makeQuery(id+"F7.imprint","IMPRINT",FACE,{"disambiguationData":[TD([[makeQuery(id+"F7.imprint","IMPRINT",EDGE,{"derivedFrom":sQuery(id+"F7.wireOp",EDGE,"E108.4.0")}),-1.0]])]});
            extrude(context, id + "F8", {"entities" : qUnion([Q0, Q1, Q2, Q3, Q4]), "oppositeDirection" : true, "depth" : .9 * mm, "offsetDistance" : 25 * mm});
        }
        {
            var Q0;
            Q0=makeQuery(id+"F3.opExtrude","CAP_FACE",FACE,{"disambiguationData":[OSD([sQuery(id+"F0.wireOp",EDGE,"E20"),sQuery(id+"F0.wireOp",EDGE,"E30")])],"isStart":false});
            var sketch = newSketch(context, id + "F9", { "sketchPlane" : qUnion([Q0])});
            skCircle(sketch, "E114.0.0", {"center": v(60, 141.34) * mm, "radius": 5 * mm});
            skCircle(sketch, "E114.2.0", {"center": v(10, -5) * mm, "radius": 5 * mm});
            skCircle(sketch, "E114.3.0", {"center": v(60, -5) * mm, "radius": 5 * mm});
            skCircle(sketch, "E115", {"center": v(10, 141.34) * mm, "radius": 6 * mm});
            skCircle(sketch, "E116", {"center": v(60, 141.34) * mm, "radius": 6 * mm});
            skCircle(sketch, "E117", {"center": v(60, -5) * mm, "radius": 6 * mm});
            skCircle(sketch, "E118", {"center": v(10, -5) * mm, "radius": 6 * mm});
            skSolve(sketch);
        }
        {
            var Q0;
            Q0=makeQuery(id+"F9.imprint","IMPRINT",FACE,{"disambiguationData":[TD([[makeQuery(id+"F9.imprint","IMPRINT",EDGE,{"derivedFrom":sQuery(id+"F9.wireOp",EDGE,"E115")}),1.0]])]});
            var Q1;
            Q1=makeQuery(id+"F9.imprint","IMPRINT",FACE,{"disambiguationData":[TD([[makeQuery(id+"F9.imprint","IMPRINT",EDGE,{"derivedFrom":sQuery(id+"F9.wireOp",EDGE,"E114.0.0")}),-1.0]])]});
            var Q2;
            Q2=makeQuery(id+"F9.imprint","IMPRINT",FACE,{"disambiguationData":[TD([[makeQuery(id+"F9.imprint","IMPRINT",EDGE,{"derivedFrom":sQuery(id+"F9.wireOp",EDGE,"E114.3.0")}),-1.0]])]});
            var Q3;
            Q3=makeQuery(id+"F9.imprint","IMPRINT",FACE,{"disambiguationData":[TD([[makeQuery(id+"F9.imprint","IMPRINT",EDGE,{"derivedFrom":sQuery(id+"F9.wireOp",EDGE,"E114.2.0")}),-1.0]])]});
            extrude(context, id + "F10", {"entities" : qUnion([Q0, Q1, Q2, Q3]), "oppositeDirection" : true, "depth" : .9 * mm, "offsetDistance" : 25 * mm});
        }
        {
            var Q0;
            Q0=makeQuery(id+"F3.opExtrude","CAP_EDGE",EDGE,{"disambiguationData":[OSD([sQuery(id+"F0.wireOp",EDGE,"E20")])],"isStart":true});
            var Q1;
            Q1=makeQuery(id+"F3.opExtrude","CAP_EDGE",EDGE,{"disambiguationData":[OSD([sQuery(id+"F0.wireOp",EDGE,"E21")])],"isStart":true});
            var Q2;
            Q2=makeQuery(id+"F2.opExtrude","CAP_EDGE",EDGE,{"disambiguationData":[OSD([sQuery(id+"F0.wireOp",EDGE,"E6")])],"isStart":true});
            var Q3;
            Q3=makeQuery(id+"F2.opExtrude","CAP_EDGE",EDGE,{"disambiguationData":[OSD([sQuery(id+"F0.wireOp",EDGE,"E7")])],"isStart":true});
            var Q4;
            Q4=makeQuery(id+"F2.opExtrude","CAP_EDGE",EDGE,{"disambiguationData":[OSD([sQuery(id+"F0.wireOp",EDGE,"E8")])],"isStart":true});
            var Q5;
            Q5=makeQuery(id+"F2.opExtrude","CAP_EDGE",EDGE,{"disambiguationData":[OSD([sQuery(id+"F0.wireOp",EDGE,"E9")])],"isStart":true});
            var Q6;
            Q6=makeQuery(id+"F2.opExtrude","CAP_EDGE",EDGE,{"disambiguationData":[OSD([sQuery(id+"F0.wireOp",EDGE,"E10")])],"isStart":true});
            var Q7;
            Q7=makeQuery(id+"F3.opExtrude","CAP_EDGE",EDGE,{"disambiguationData":[OSD([sQuery(id+"F0.wireOp",EDGE,"E25")])],"isStart":true});
            var Q8;
            Q8=makeQuery(id+"F3.opExtrude","CAP_EDGE",EDGE,{"disambiguationData":[OSD([sQuery(id+"F0.wireOp",EDGE,"E26")])],"isStart":true});
            var Q9;
            Q9=makeQuery(id+"F1.opExtrude","SWEPT_EDGE",EDGE,{"disambiguationData":[OSD([sQuery(id+"F0.wireOp",EDGE,"E0.bottom"),sQuery(id+"F0.wireOp",EDGE,"E0.left"),sQuery(id+"F0.wireOp",EDGE,"E27")])]});
            var Q10;
            Q10=makeQuery(id+"F1.opExtrude","SWEPT_EDGE",EDGE,{"disambiguationData":[OSD([sQuery(id+"F0.wireOp",EDGE,"E0.bottom"),sQuery(id+"F0.wireOp",EDGE,"E0.right"),sQuery(id+"F0.wireOp",EDGE,"E28")])]});
            var Q11;
            Q11=makeQuery(id+"F1.opExtrude","SWEPT_EDGE",EDGE,{"disambiguationData":[OSD([sQuery(id+"F0.wireOp",EDGE,"E0.top"),sQuery(id+"F0.wireOp",EDGE,"E0.right"),sQuery(id+"F0.wireOp",EDGE,"E23")])]});
            var Q12;
            Q12=makeQuery(id+"F1.opExtrude","SWEPT_EDGE",EDGE,{"disambiguationData":[OSD([sQuery(id+"F0.wireOp",EDGE,"E0.top"),sQuery(id+"F0.wireOp",EDGE,"E0.left"),sQuery(id+"F0.wireOp",EDGE,"E22")])]});
            var Q13;
            Q13=makeQuery(id+"F10.opExtrude","CAP_EDGE",EDGE,{"disambiguationData":[OSD([sQuery(id+"F0.wireOp",EDGE,"E20")])],"isStart":false});
            var Q14;
            Q14=makeQuery(id+"F10.opExtrude","CAP_EDGE",EDGE,{"disambiguationData":[OSD([sQuery(id+"F9.wireOp",EDGE,"E114.0.0")])],"isStart":false});
            var Q15;
            Q15=makeQuery(id+"F10.opExtrude","CAP_EDGE",EDGE,{"disambiguationData":[OSD([sQuery(id+"F9.wireOp",EDGE,"E114.2.0")])],"isStart":false});
            var Q16;
            Q16=makeQuery(id+"F10.opExtrude","CAP_EDGE",EDGE,{"disambiguationData":[OSD([sQuery(id+"F9.wireOp",EDGE,"E114.3.0")])],"isStart":false});
            var Q17;
            Q17=makeQuery(id+"F8.opExtrude","CAP_EDGE",EDGE,{"disambiguationData":[OSD([sQuery(id+"F0.wireOp",EDGE,"E6")])],"isStart":false});
            var Q18;
            Q18=makeQuery(id+"F8.opExtrude","CAP_EDGE",EDGE,{"disambiguationData":[OSD([sQuery(id+"F7.wireOp",EDGE,"E108.1.0")])],"isStart":false});
            var Q19;
            Q19=makeQuery(id+"F8.opExtrude","CAP_EDGE",EDGE,{"disambiguationData":[OSD([sQuery(id+"F7.wireOp",EDGE,"E108.4.0")])],"isStart":false});
            var Q20;
            Q20=makeQuery(id+"F8.opExtrude","CAP_EDGE",EDGE,{"disambiguationData":[OSD([sQuery(id+"F7.wireOp",EDGE,"E108.2.0")])],"isStart":false});
            var Q21;
            Q21=makeQuery(id+"F8.opExtrude","CAP_EDGE",EDGE,{"disambiguationData":[OSD([sQuery(id+"F7.wireOp",EDGE,"E108.3.0")])],"isStart":false});
            fillet(context, id + "F11", {"entities" : qUnion([Q0, Q1, Q2, Q3, Q4, Q5, Q6, Q7, Q8, Q9, Q10, Q11, Q12, Q13, Q14, Q15, Q16, Q17, Q18, Q19, Q20, Q21]), "radius" : 3 * mm, "tangentPropagation" : true, "allowEdgeOverflow" : false});
        }
    });
